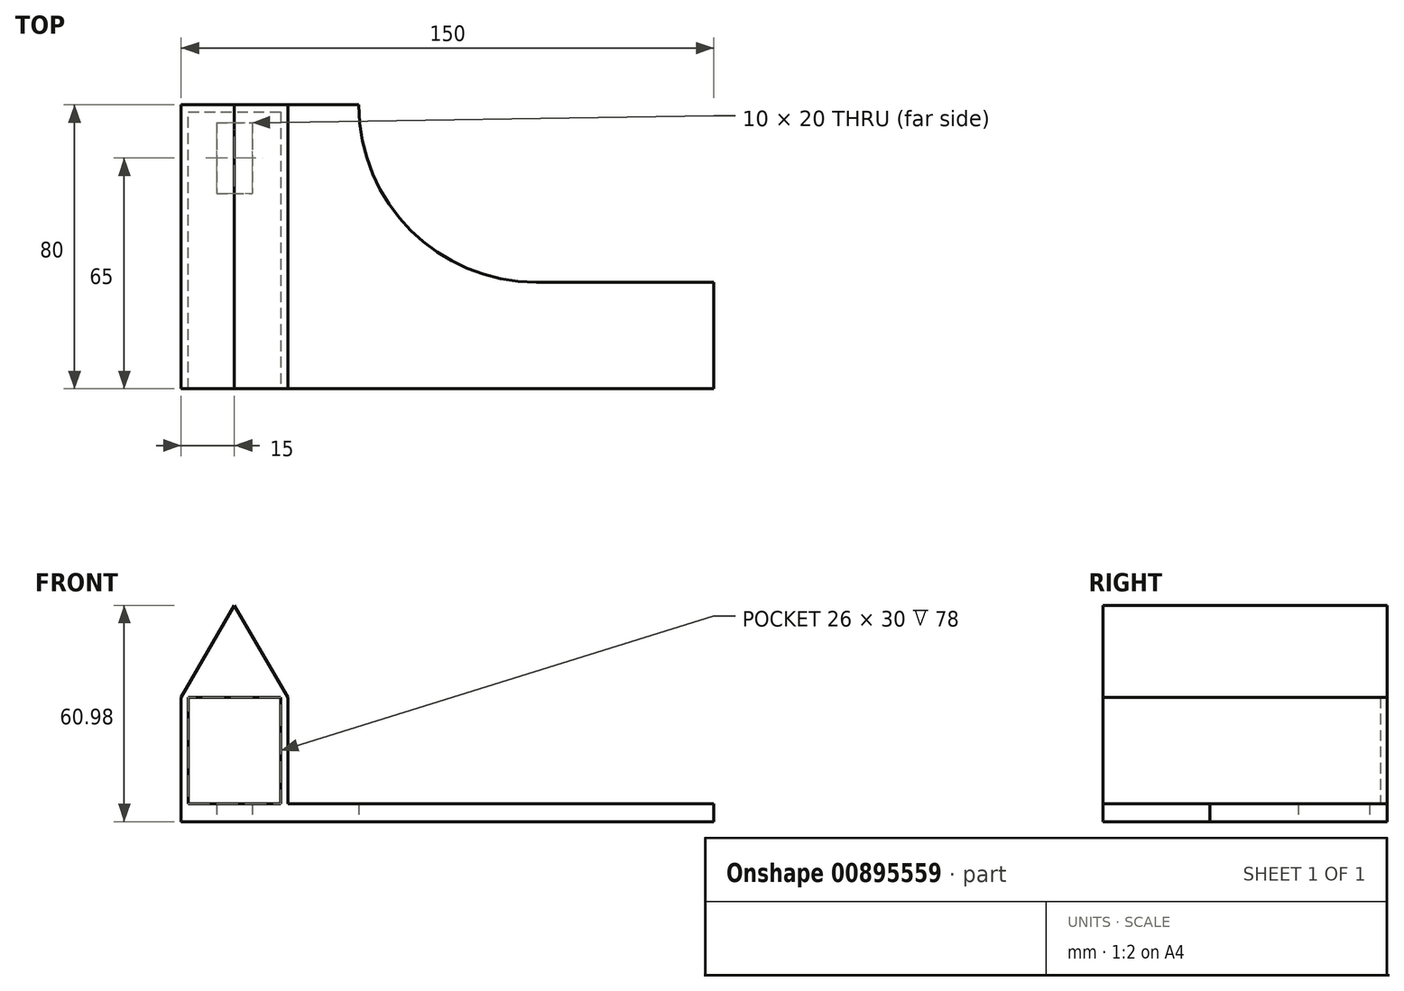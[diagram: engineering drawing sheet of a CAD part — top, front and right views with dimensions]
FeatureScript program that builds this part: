
annotation { "Feature Type Name" : "Feature", "Feature Type Description" : "" }
export const myFeature = defineFeature(function(context is Context, id is Id, definition is map)
    precondition{}
    {
        {
            var Q0;
            Q0=qCreatedBy(makeId("Top.planeOp"),FACE);
            var sketch = newSketch(context, id + "F0", { "sketchPlane" : qUnion([Q0])});
            skLineSegment(sketch, "E0", {"start": v(100, -25) * mm, "end": v(150, -25) * mm});
            skLineSegment(sketch, "E1", {"start": v(150, -25) * mm, "end": v(150, -55) * mm});
            skLineSegment(sketch, "E2", {"start": v(150, -55) * mm, "end": v(0, -55) * mm});
            skLineSegment(sketch, "E3", {"start": v(0, -55) * mm, "end": v(0, 25) * mm});
            skLineSegment(sketch, "E4", {"start": v(0, 25) * mm, "end": v(50, 25) * mm});
            skLineSegment(sketch, "E5", {"start": v(50, 25) * mm, "end": v(50, 25) * mm});
            skPoint(sketch, "E6.newPointA", {"position": v(50, -75.36) * mm});
            skArc(sketch, "E6.filletArc", {"start": v(50, 25) * mm, "mid": v(64.64, -10.36) * mm, "end": v(100, -25) * mm});
            skLineSegment(sketch, "E7.bottom", {"start": v(10, 20) * mm, "end": v(20, 20) * mm});
            skLineSegment(sketch, "E7.top", {"start": v(10, 0) * mm, "end": v(20, 0) * mm});
            skLineSegment(sketch, "E7.left", {"start": v(10, 20) * mm, "end": v(10, 0) * mm});
            skLineSegment(sketch, "E7.right", {"start": v(20, 20) * mm, "end": v(20, 0) * mm});
            skSolve(sketch);
        }
        {
            var Q0;
            Q0 = qSketchRegion(id + "F0", true);
            extrude(context, id + "F1", {"entities" : qUnion([Q0]), "depth" : 5 * mm, "offsetDistance" : 25.4 * mm});
        }
        {
            var Q0;
            Q0=makeQuery(id+"F1.opExtrude","CAP_FACE",FACE,{"disambiguationData":[OSD([sQuery(id+"F0.wireOp",EDGE,"E0"),sQuery(id+"F0.wireOp",EDGE,"E1"),sQuery(id+"F0.wireOp",EDGE,"E2"),sQuery(id+"F0.wireOp",EDGE,"E3"),sQuery(id+"F0.wireOp",EDGE,"E4"),sQuery(id+"F0.wireOp",EDGE,"E6.filletArc"),sQuery(id+"F0.wireOp",EDGE,"E7.bottom"),sQuery(id+"F0.wireOp",EDGE,"E7.top"),sQuery(id+"F0.wireOp",EDGE,"E7.left"),sQuery(id+"F0.wireOp",EDGE,"E7.right")])],"isStart":false});
            var sketch = newSketch(context, id + "F2", { "sketchPlane" : qUnion([Q0])});
            skLineSegment(sketch, "E8", {"start": v(0, 25) * mm, "end": v(30, 25) * mm});
            skLineSegment(sketch, "E9", {"start": v(30, 25) * mm, "end": v(30, -55) * mm});
            skLineSegment(sketch, "E10", {"start": v(0, -55) * mm, "end": v(0, 25) * mm});
            skLineSegment(sketch, "E11", {"start": v(2, -55) * mm, "end": v(2, 23) * mm});
            skLineSegment(sketch, "E12", {"start": v(2, 23) * mm, "end": v(28, 23) * mm});
            skLineSegment(sketch, "E13", {"start": v(28, 23) * mm, "end": v(28, -55) * mm});
            skLineSegment(sketch, "E14", {"start": v(28, -55) * mm, "end": v(30, -55) * mm});
            skLineSegment(sketch, "E15", {"start": v(2, -55) * mm, "end": v(0, -55) * mm});
            skSolve(sketch);
        }
        {
            var Q0;
            Q0 = qSketchRegion(id + "F2", true);
            extrude(context, id + "F3", {"entities" : qUnion([Q0]), "operationType" : NewBodyOperationType.ADD, "depth" : 30 * mm, "offsetDistance" : 25.4 * mm});
        }
        {
            var Q0;
            Q0=makeQuery(id+"F3.boolean.opBoolean","MERGE",FACE,{"derivedFrom":[makeQuery(id+"F1.opExtrude","SWEPT_FACE",FACE,{"disambiguationData":[OSD([sQuery(id+"F0.wireOp",EDGE,"E4")])]}),makeQuery(id+"F3.opExtrude","SWEPT_FACE",FACE,{"disambiguationData":[OSD([sQuery(id+"F2.wireOp",EDGE,"E8")])]})]});
            var sketch = newSketch(context, id + "F4", { "sketchPlane" : qUnion([Q0])});
            skLineSegment(sketch, "E16", {"start": v(-30, 35) * mm, "end": v(-15, 60.98) * mm});
            skLineSegment(sketch, "E17", {"start": v(-15, 60.98) * mm, "end": v(0, 35) * mm});
            skLineSegment(sketch, "E18", {"start": v(0, 35) * mm, "end": v(-30, 35) * mm});
            skSolve(sketch);
        }
        {
            var Q0;
            Q0 = qSketchRegion(id + "F4", true);
            var Q1;
            Q1=makeQuery(id+"F3.boolean.opBoolean","MERGE",FACE,{"derivedFrom":[makeQuery(id+"F1.opExtrude","SWEPT_FACE",FACE,{"disambiguationData":[OSD([sQuery(id+"F0.wireOp",EDGE,"E2")])]}),makeQuery(id+"F3.opExtrude","SWEPT_FACE",FACE,{"disambiguationData":[OSD([sQuery(id+"F2.wireOp",EDGE,"E14")])]}),makeQuery(id+"F3.opExtrude","SWEPT_FACE",FACE,{"disambiguationData":[OSD([sQuery(id+"F2.wireOp",EDGE,"E15")])]})]});
            extrude(context, id + "F5", {"entities" : qUnion([Q0]), "operationType" : NewBodyOperationType.ADD, "endBound" : BoundingType.UP_TO_SURFACE, "oppositeDirection" : true, "depth" : 72.9 * mm, "endBoundEntityFace" : qUnion([Q1]), "offsetDistance" : 25.4 * mm});
        }
    });
